# Revit family: QF_Vollrath_3664430_cat
name_source: partatom
category: Specialty Equipment
revit_build: Autodesk Revit 2016 (Build: 20151007_0715(x64)
units: mm (PartAtom-declared; Revit-internal decimal feet)

## family parameters
Always vertical = Yes
Cut with Voids When Loaded = No
OmniClass Number = 23.40.40.14.14
OmniClass Title = Food Preparation Equipment
Part Type = Normal
Room Calculation Point = No
Round Connector Dimension = Use Radius
Shared = No
Work Plane-Based = No

## types (1)
- QF_Vollrath_3664430_cat
    AF Apparent Power = 24 VA
    AF Cold Water Size = 0"
    AF Conn Plug = NEMA 5-15P
    AF Cycle = 60 Hz
    AF FL Amps = 0 A
    AF Indirect Waste Size = 0"
    AF Phase = 1
    AF Volts = 120 V
    AF Watts = 16 W
    Actual Weight = 0
    Apparent Power = 0 VA
    Assembly Code = E1090320
    Auto Fill = No
    CSI MasterFormat = 11 42 00
    Conn Plug = -
    Cycle = 60 Hz
    Depth = 1' - 6"
    Description = Short Side Hot Drop-in
    FL Amps = 0 A
    Height = 1' - 9"
    Indirect Waste Size = 1"
    Length = 0' - 0"
    Manufacturer = Vollrath
    Model = -
    Number of Poles = 1
    Phase = 0
    URL = www.vollrathco.com
    Volts = 0 V
    Watts = 0 W
    Weight in Pounds = 0
    Width = 7' - 4 9/16"

## geometry (parser evidence)
native form markers: Blend x10, Sweep x5
no freeform markers — native parametric forms only
